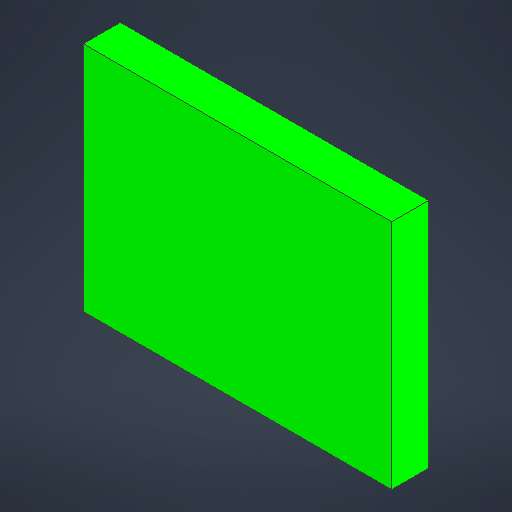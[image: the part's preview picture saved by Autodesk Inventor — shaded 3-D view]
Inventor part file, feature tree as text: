
AUTODESK INVENTOR PART (.ipt)
format: ipt  version: 2025.2 (Build 292293000, 293)  size: 178,176 bytes
history: native  units: in
note: dims shown in document units (in); Inventor stores cm internally (conversion verified against a paired STEP export)
features: reference x5, other x3, extrude x1, sketch x1
ambient origin geometry x8: Origin, YZ Plane, XZ Plane, XY Plane, X Axis, Y Axis, Z Axis, Center Point
bodies: Solid1 (feature_tree)
feature tree (10):
  extrude  "Extrusion1"  [1 undecoded]
  sketch  "Sketch1"  dims[d0=0.7874in d1=0.0in]
  reference  "Reference1"
  reference  "Reference2"
  reference  "Reference3"
  reference  "Reference4"
  reference  "Reference5"
  other  "18650ASSEMBLYfordrawing.iam"
  other  "PILLARSCELLCASE18650:1"
  other  "cooling plate:1"
note: 1 required parameter value undecoded (feature->parameter linkage not recoverable at this tier; creation-order binding heuristic only, values carry confidence <= 0.55)
